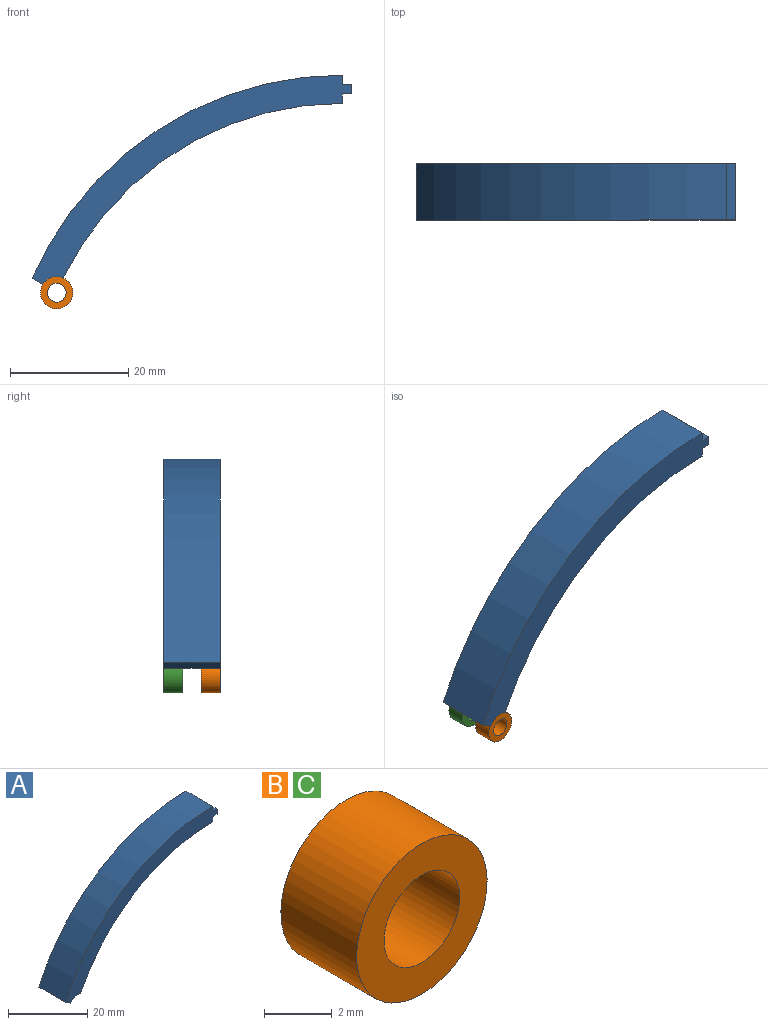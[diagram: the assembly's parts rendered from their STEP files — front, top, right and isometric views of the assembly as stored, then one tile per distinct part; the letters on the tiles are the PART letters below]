
ASSEMBLY  parts=3 mates=2
PART A: 11 faces, bbox 54x9.5x35.4 mm
  f0: plane 9.53x1.59mm, normal (1,0,0), area 15.1mm2, adj f1,f8,f9,f10
  f1: plane 9.53x1.59mm, normal (0,0,-1), area 15.1mm2, adj f0,f2,f9,f10
  f2: plane 9.53x1.59mm, normal (1,0,0), area 15.1mm2, adj f1,f3,f9,f10
  f3: plane 9.53x1.59mm, normal (0,0,1), area 15.1mm2, adj f2,f4,f9,f10
  f4: plane 9.53x1.59mm, normal (1,0,0), area 15.1mm2, adj f3,f5,f9,f10
  f5: cylinder r=57.15mm len=52.39mm, axis (0,1,0), area 631.3mm2, adj f4,f6,f9,f10
  f6: plane 9.53x1.78mm, normal (-0.51,0,-0.86), area 19.8mm2, adj f5,f7,f9,f10
  f7: cylinder r=2.73mm len=9.53mm, axis (0,1,0), area 38mm2, adj f6,f8,f9,f10
  f8: cylinder r=52.39mm len=47.13mm, axis (0,1,0), area 558.4mm2, adj f0,f7,f9,f10
  f9: plane 53.98x35.37mm, normal (0,-1,0), area 301mm2, adj f0,f1,f2,f3,f4,f5,f6,f7
  f10: plane 53.98x35.37mm, normal (0,1,0), area 301mm2, adj f0,f1,f2,f3,f4,f5,f6,f7
PART B: 4 faces, bbox 5.5x3.2x5.5 mm
  f0: cylinder r=1.59mm len=3.18mm, axis (0,1,0), area 31.7mm2, adj f2,f3
  f1: cylinder r=2.73mm len=5.46mm, axis (0,1,0), area 54.5mm2, adj f2,f3
  f2: plane 5.46x5.46mm, normal (0,-1,0), area 15.5mm2, adj f0,f1
  f3: plane 5.46x5.46mm, normal (0,1,0), area 15.5mm2, adj f0,f1
PART C: same geometry as B
PLACE A t=(15,-6.91,-0.82)mm
PLACE B t=(-31.59,-13.26,-21.08)mm
PLACE C t=(-31.59,-6.91,-21.08)mm
MATE fastened C.f0 <-> A.f7  axis (0,1,0) through (-31.59,-6.91,-21.08)mm
MATE fastened B.f1 <-> A.f7  axis (0,-1,0) through (-31.59,-16.44,-21.08)mm
